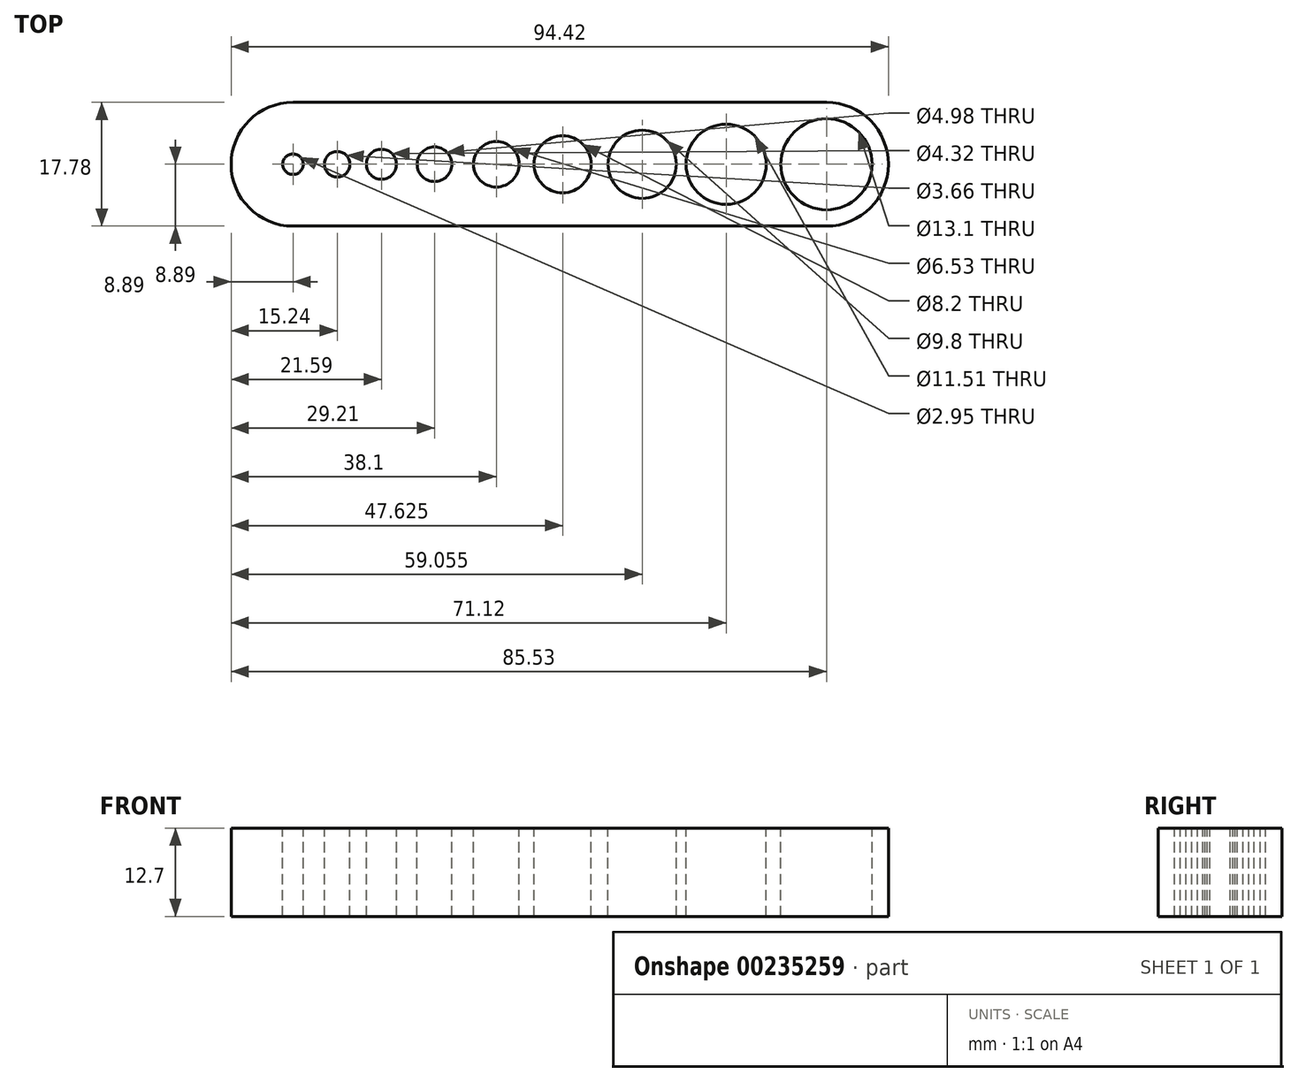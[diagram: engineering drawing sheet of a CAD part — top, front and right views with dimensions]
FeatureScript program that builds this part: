
annotation { "Feature Type Name" : "Feature", "Feature Type Description" : "" }
export const myFeature = defineFeature(function(context is Context, id is Id, definition is map)
    precondition{}
    {
        {
            var Q0;
            Q0=qCreatedBy(makeId("Top.planeOp"),FACE);
            var sketch = newSketch(context, id + "F0", { "sketchPlane" : qUnion([Q0])});
            skLineSegment(sketch, "E0", {"start": v(0, 8.9) * mm, "end": v(76.64, 8.9) * mm, "construction": true});
            skCircle(sketch, "E1", {"center": v(0, 8.9) * mm, "radius": 8.9 * mm});
            skCircle(sketch, "E2", {"center": v(76.64, 8.9) * mm, "radius": 8.9 * mm});
            skLineSegment(sketch, "E3", {"start": v(0, 17.78) * mm, "end": v(76.64, 17.78) * mm});
            skLineSegment(sketch, "E4", {"start": v(0, 0) * mm, "end": v(76.64, 0) * mm});
            skSolve(sketch);
        }
        {
            var Q0;
            Q0 = qSketchRegion(id + "F0", true);
            extrude(context, id + "F1", {"entities" : qUnion([Q0]), "depth" : 12.7 * mm});
        }
        {
            var Q0;
            Q0=makeQuery(id+"F1.opExtrude","CAP_FACE",FACE,{"disambiguationData":[OSD([sQuery(id+"F0.wireOp",EDGE,"E1"),sQuery(id+"F0.wireOp",EDGE,"E2"),sQuery(id+"F0.wireOp",EDGE,"E3"),sQuery(id+"F0.wireOp",EDGE,"E4")])],"isStart":false});
            var sketch = newSketch(context, id + "F2", { "sketchPlane" : qUnion([Q0])});
            skCircle(sketch, "E5", {"center": v(0, 8.9) * mm, "radius": 1.47 * mm});
            skCircle(sketch, "E6", {"center": v(76.64, 8.9) * mm, "radius": 6.55 * mm});
            skCircle(sketch, "E7", {"center": v(6.35, 8.9) * mm, "radius": 1.83 * mm});
            skCircle(sketch, "E8", {"center": v(12.7, 8.9) * mm, "radius": 2.16 * mm});
            skCircle(sketch, "E9", {"center": v(20.32, 8.9) * mm, "radius": 2.49 * mm});
            skCircle(sketch, "E10", {"center": v(29.21, 8.9) * mm, "radius": 3.26 * mm});
            skCircle(sketch, "E11", {"center": v(38.73, 8.9) * mm, "radius": 4.1 * mm});
            skCircle(sketch, "E12", {"center": v(50.16, 8.9) * mm, "radius": 4.9 * mm});
            skCircle(sketch, "E13", {"center": v(62.23, 8.9) * mm, "radius": 5.75 * mm});
            skSolve(sketch);
        }
        {
            var Q0;
            Q0 = qSketchRegion(id + "F2", true);
            extrude(context, id + "F3", {"entities" : qUnion([Q0]), "operationType" : NewBodyOperationType.REMOVE, "endBound" : BoundingType.THROUGH_ALL, "oppositeDirection" : true, "depth" : 25.4 * mm});
        }
    });
